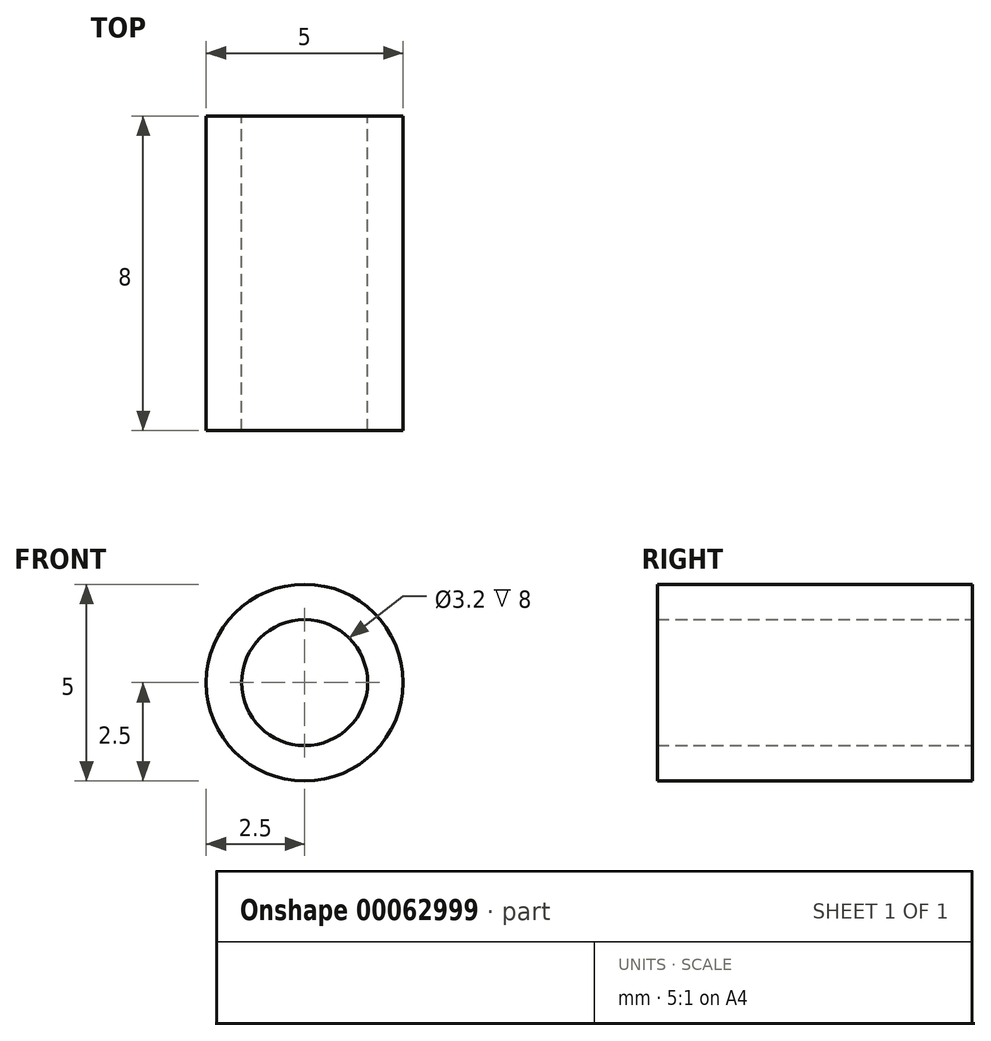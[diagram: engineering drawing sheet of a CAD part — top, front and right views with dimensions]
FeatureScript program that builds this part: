
annotation { "Feature Type Name" : "Feature", "Feature Type Description" : "" }
export const myFeature = defineFeature(function(context is Context, id is Id, definition is map)
    precondition{}
    {
        {
            var Q0;
            Q0=qCreatedBy(makeId("Front.planeOp"),FACE);
            var sketch = newSketch(context, id + "F0", { "sketchPlane" : qUnion([Q0])});
            skCircle(sketch, "E0", {"center": v(0, 0) * mm, "radius": 2.5 * mm});
            skCircle(sketch, "E1", {"center": v(0, 0) * mm, "radius": 1.6 * mm});
            skSolve(sketch);
        }
        {
            var Q0;
            Q0=makeQuery(id+"F0.imprint","IMPRINT",FACE,{"disambiguationData":[TD([[makeQuery(id+"F0.imprint","IMPRINT",EDGE,{"derivedFrom":sQuery(id+"F0.wireOp",EDGE,"E0")}),1.0]])]});
            extrude(context, id + "F1", {"entities" : qUnion([Q0]), "depth" : 8 * mm});
        }
    });
